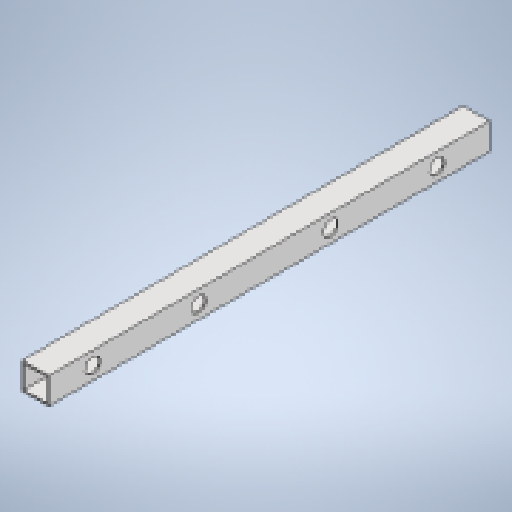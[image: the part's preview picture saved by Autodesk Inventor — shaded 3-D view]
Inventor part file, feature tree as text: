
AUTODESK INVENTOR PART (.ipt)
format: ipt  version: 2025.1 (Build 291241020, 241B)  size: 307,200 bytes
history: native  units: mm
features: extrude x2, sketch x2, projected_geometry x1
ambient origin geometry x8: Origin, YZ Plane, XZ Plane, XY Plane, X Axis, Y Axis, Z Axis, Center Point
bodies: Body1 (feature_tree)
feature tree (5):
  extrude  "Extrusion3"  Depth=30.0mm
  extrude  "Extrusion4"  Depth=2.0mm
  sketch  "Sketch9"  dims[d61=500.0mm d172=30.0mm]
  sketch  "Sketch10"  dims[d173=30.0mm d174=2.0mm d175=470.0mm d176=0.0mm d177=17.0mm d178=17.0mm d179=0.0mm d180=0.0mm d181=30.0mm d182=90.0mm d183=220.0mm d184=350.0mm d185=480.0mm d186=17.0mm]
  projected_geometry  "Projected Loop3"
